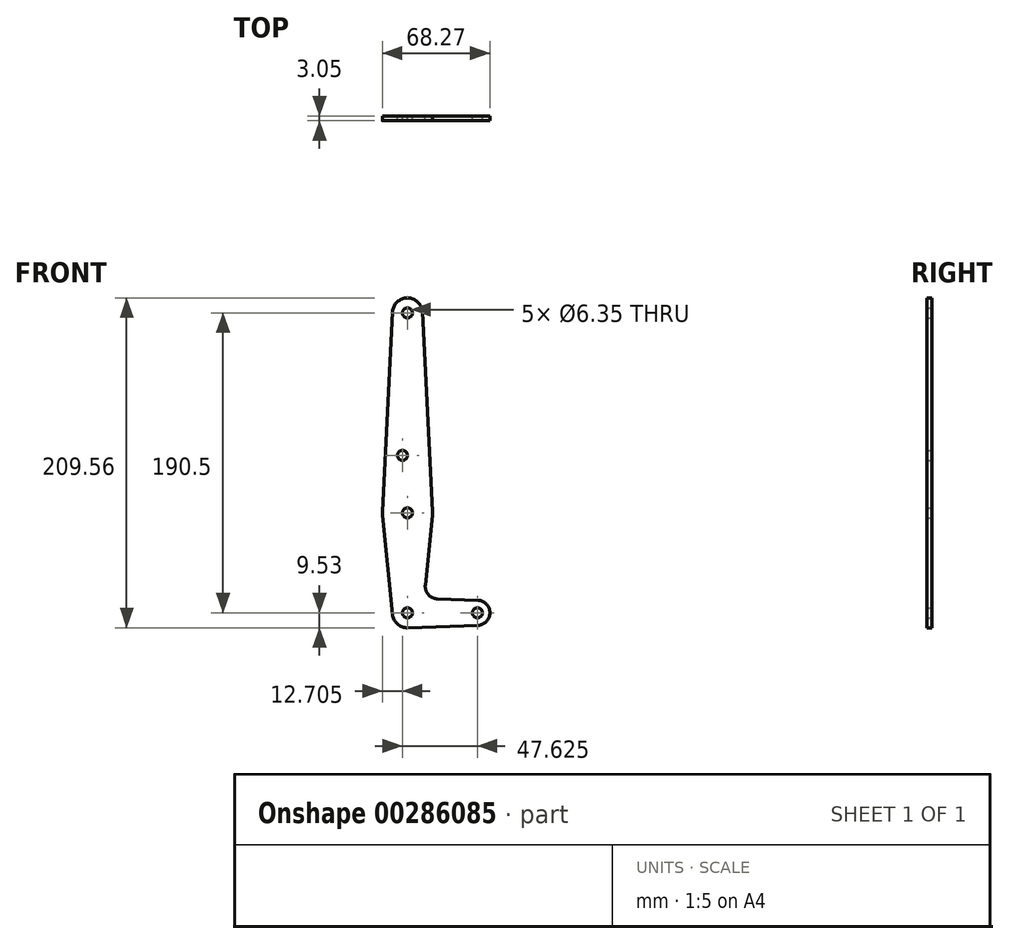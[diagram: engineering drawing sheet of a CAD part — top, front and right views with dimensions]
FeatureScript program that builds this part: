
annotation { "Feature Type Name" : "Feature", "Feature Type Description" : "" }
export const myFeature = defineFeature(function(context is Context, id is Id, definition is map)
    precondition{}
    {
        {
            var Q0;
            Q0=qCreatedBy(makeId("Front.planeOp"),FACE);
            var sketch = newSketch(context, id + "F0", { "sketchPlane" : qUnion([Q0])});
            skCircle(sketch, "E0", {"center": v(0, 0) * mm, "radius": 15.88 * mm});
            skCircle(sketch, "E1", {"center": v(0, 127) * mm, "radius": 9.53 * mm});
            skCircle(sketch, "E2", {"center": v(0, -63.5) * mm, "radius": 9.53 * mm});
            skLineSegment(sketch, "E3", {"start": v(0, 127) * mm, "end": v(0, -63.5) * mm, "construction": true});
            skLineSegment(sketch, "E4", {"start": v(0, 0) * mm, "end": v(0, -63.5) * mm, "construction": true});
            skLineSegment(sketch, "E5", {"start": v(-9.51, 127.48) * mm, "end": v(-15.86, 0.8) * mm});
            skLineSegment(sketch, "E6", {"start": v(9.51, 127.48) * mm, "end": v(15.86, 0.8) * mm});
            skLineSegment(sketch, "E7", {"start": v(-9.48, -64.45) * mm, "end": v(-15.8, -1.59) * mm});
            skLineSegment(sketch, "E8", {"start": v(15.8, -1.59) * mm, "end": v(11.34, -45.9) * mm});
            skCircle(sketch, "E9", {"center": v(44.45, -63.5) * mm, "radius": 7.94 * mm});
            skLineSegment(sketch, "E10", {"start": v(44.45, -63.5) * mm, "end": v(0, -63.5) * mm, "construction": true});
            skLineSegment(sketch, "E11", {"start": v(44.73, -71.43) * mm, "end": v(0.34, -73.02) * mm});
            skCircle(sketch, "E12", {"center": v(-3.17, 36.53) * mm, "radius": 3.18 * mm});
            skLineSegment(sketch, "E13", {"start": v(0, 0) * mm, "end": v(0, 36.53) * mm, "construction": true});
            skLineSegment(sketch, "E14", {"start": v(18.97, -54.65) * mm, "end": v(44.73, -55.57) * mm});
            skArc(sketch, "E15.filletArc", {"start": v(11.34, -45.9) * mm, "mid": v(13.26, -51.93) * mm, "end": v(18.97, -54.65) * mm});
            skCircle(sketch, "E16", {"center": v(0, 127) * mm, "radius": 3.18 * mm});
            skCircle(sketch, "E17", {"center": v(0, 0) * mm, "radius": 3.18 * mm});
            skCircle(sketch, "E18", {"center": v(0, -63.5) * mm, "radius": 3.18 * mm});
            skCircle(sketch, "E19", {"center": v(44.45, -63.5) * mm, "radius": 3.18 * mm});
            skSolve(sketch);
        }
        {
            var Q0;
            {var subQ1=sQuery(id+"F0.wireOp",EDGE,"E7");Q0=makeQuery(id+"F0.imprint","IMPRINT",FACE,{"disambiguationData":[TD([[makeQuery(id+"F0.imprint","IMPRINT",EDGE,{"derivedFrom":subQ1}),-1.0]])]});}
            var Q1;
            Q1=makeQuery(id+"F0.imprint","IMPRINT",FACE,{"disambiguationData":[TD([[makeQuery(id+"F0.imprint","IMPRINT",EDGE,{"derivedFrom":sQuery(id+"F0.wireOp",EDGE,"E17")}),-1.0]])]});
            var Q2;
            {var subQ1=sQuery(id+"F0.wireOp",EDGE,"E5");Q2=makeQuery(id+"F0.imprint","IMPRINT",FACE,{"disambiguationData":[TD([[makeQuery(id+"F0.imprint","IMPRINT",EDGE,{"derivedFrom":subQ1}),1.0]])]});}
            var Q3;
            Q3=makeQuery(id+"F0.imprint","IMPRINT",FACE,{"disambiguationData":[TD([[makeQuery(id+"F0.imprint","IMPRINT",EDGE,{"derivedFrom":sQuery(id+"F0.wireOp",EDGE,"E16")}),-1.0]])]});
            var Q4;
            Q4=makeQuery(id+"F0.imprint","IMPRINT",FACE,{"disambiguationData":[TD([[makeQuery(id+"F0.imprint","IMPRINT",EDGE,{"derivedFrom":sQuery(id+"F0.wireOp",EDGE,"E18")}),-1.0]])]});
            var Q5;
            Q5=makeQuery(id+"F0.imprint","IMPRINT",FACE,{"disambiguationData":[TD([[makeQuery(id+"F0.imprint","IMPRINT",EDGE,{"derivedFrom":sQuery(id+"F0.wireOp",EDGE,"E19")}),-1.0]])]});
            extrude(context, id + "F1", {"entities" : qUnion([Q0, Q1, Q2, Q3, Q4, Q5]), "depth" : 3.05 * mm});
        }
    });
